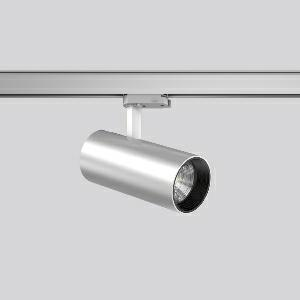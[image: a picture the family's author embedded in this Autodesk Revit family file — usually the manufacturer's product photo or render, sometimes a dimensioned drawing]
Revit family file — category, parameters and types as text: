
# Revit family: deecos_s_mini_742207_004_3_76_1f53
name_source: partatom
category: Lighting Fixtures
units: mm (PartAtom-declared; Revit-internal decimal feet)

## family parameters
Cut with Voids When Loaded = No
Host = Face
Light Source = No
Part Type = Normal
Room Calculation Point = No
Round Connector Dimension = Use Diameter
Shared = No

## types (1)
- DEECOS S mini (1 x LED Modul 935, 3050 lm, 3500)
    Apparent Load = 29 VA
    Approval mark = CE
    CIE Flux Codes = 96 100 100 100 100
    Color Rendering = 92
    Color Temperature = 3500
    Default Elevation = 1800 mm
    Description = Series: DEECOS S mini
LED surface-mounted projector in modern design with no visible cooling ribs. Housing: die-cast aluminium, powder-coated. Rotation range: 356°. Swivel range: 90°. Black plastic ring and recessed LED to prevent glare from the side. Optical assembly with lens made of plastic (polycarbonate) for the best homogeneous light distribution - can be changed without tools. Best colour rendering index Ra>90. With adapter for RZB 3-circuit DALI tracks. Suitable for Track on ceiling, Wall track. High quality converter without flickering and stroboscopic effect. The following accessories can be mounted without use of tools: interchangeable lenses, decorative glasses, honeycomb louvre, clear and frosted diffusers, white interchangeable plastic ring. 
Colour: silver
Diameter: 87 mm
Height: 214 mm
Lamp: LED
Socket: without socket
Colour temperature: 3500K
Colour rendering index (CRI): 92
System power: 29 W
Rated luminous flux: 3050 lm
Luminous efficiency: 105 lm/W
Control gear: Converter, dimmable, DALI
Protection class: I
Type of protection: IP 20
    Height = 214 mm
    Lamp = 1 x LED Modul 935
    Lamp Light Flux = 3050 lm
    Lamp count = 1
    Length = 87 mm
    Lifetime = 50000 h
    Luminous efficacy = 105 lm/W
    Manufacturer = RZB
    ModVariant = No
    Model = 742207.004.3.76
    Mounting Place = Ceiling
    Mounting Type = Rail mounted
    Number of Poles = 1
    OnlyDefault = Yes
    Power Factor = 1
    Product Name = DEECOS S mini
    Product group = Track mounted projectors
    ProductGroupID = 301
    Protection Class = Protection class I
    Protection Degree = IP 20
    RLX_Detail_Level = 1
    RLX_Emergency_Light_Flux = 0 lm
    RLX_Emergency_Type = 0
    RLX_Emergency_Type_DB = No
    RlxData = <blob elided: 37013 chars, md5=93494c35>
    Socket = socket
    Standby Power = 0 W
    System Light Flux = 3050 lm
    System Power = 29 W
    Type Comments = Product without accessories
    Type Image = 741930.004.jpg
    URL = http://relux.com
    VarID = ---
    Voltage = 230 V
    Voltage Range = 220-240 V
    Weight = 0.00 kg
    Width = 0 mm  [stored 0 ft]

note: [stored X ft] marks values corroborated as IEEE doubles in the binary element streams (Revit-internal decimal feet)

## geometry (parser evidence)
native form markers: Blend x4, Sweep x12
no freeform markers — native parametric forms only
